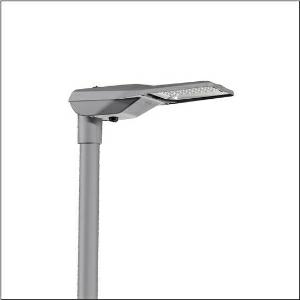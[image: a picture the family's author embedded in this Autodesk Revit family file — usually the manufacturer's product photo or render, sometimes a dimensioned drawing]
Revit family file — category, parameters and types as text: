
# Revit family: streetlight_sl_21_mini___st0_8a_5xe2c43t08jb_d1cf
name_source: partatom
category: Lighting Fixtures
units: mm (PartAtom-declared; Revit-internal decimal feet)

## family parameters
Cut with Voids When Loaded = No
Host = Face
Light Source = No
Part Type = Normal
Room Calculation Point = No
Round Connector Dimension = Use Diameter
Shared = No

## types (1)
- --- (1 x LED, 13500 lm, 88.6 W, 4000K)
    Apparent Load = 89 VA
    CIE Flux Codes = 41 75 97 100 100
    Color Rendering = 70
    Color Temperature = 4000K
    Default Elevation = 1800 mm
    Description = Streetlight SL 21 mini, mast luminaire, primary light control with lens, of PMMA, primary optical cover: cover, of toughened safety glass, transparent, light distribution: ST0.8a, light emission: direct distribution, primary light characteristic: asymmetric, installation type: side-entry, post-top, LED, High Power LED, rated luminous flux: 13.500lm, luminous efficacy: 152lm/W, light colour: 740, colour temperature: 4000K, control gear: D4i, control: overheat protection, constant luminous flux control, time-dependent luminous flux control, flexible luminous flux parameterisation, pre-setting: logarithmic dimming characteristic, mains connection: 220..240V, AC, 50/60Hz, start of lifetime: 89W, end of service life: 92W, reduction: 41W, luminaire housing, of diecast aluminium, powder-coated, Siteco® metallic grey (DB 702S), corrosivity category C5 mid according to DIN EN ISO 12944, please order mast flange separately, inclination adjustable: 0°, 5°, 10°, 15°, sealing non-destructively replaceable, multi-level sealing system, length: 628mm, width: 235mm, height: 110mm, mast flange for spigot size: 42mm (side-entry): 5XC10008XM4, 60/48mm (side-entry/post-top): 5XC10108XM2, 76/60mm (side-entry/post-top): 5XC10108XM1, mounting height: 4..8m, Smart Interface below and above, protection rating (complete): IP66, insulation class (complete): insulation class II (safety insulation), certification: CE, ENEC, ENEC+, VDE, impact resistance: IK10, permissible operating ambient temperature for outdoor applications: -40..+50°C, standard-compliant lighting for roads and squares, packaging unit: 1 piece

Light Distribution: ST0.8a
    Height = 110 mm
    Lamp = 1 x LED
    Lamp Light Flux = 13500 lm
    Lamp Power = 88.6 W
    Lamp count = 1
    Length = 625 mm
    Luminous efficacy = 152 lm/W
    Manufacturer = Siteco
    ModVariant = No
    Model = 5XE2C43T08JB
    Number of Poles = 1
    OnlyDefault = Yes
    Power Factor = 1
    Product Name = Streetlight SL 21 mini | ST0.8a
    Product group = mast luminaire | pylon top
    ProductGroupID = 6100
    Protection Class = Protection class II
    Protection Degree = IP 66
    RLX_Detail_Level = 1
    RLX_Emergency_Light_Flux = 0 lm
    RLX_Emergency_Type = 0
    RLX_Emergency_Type_DB = No
    RlxData = <blob elided: 26341 chars, md5=08f5da4b>
    Socket = socket
    Standby Power = 0 W
    System Light Flux = 13500 lm
    System Power = 89 W
    Type Comments = factory setting: luminous flux: 100 % | dim-lin: 254 | 915 mA
    Type Image = l_1003514.jpg
    URL = http://relux.com
    VarID = @adj_031021
    Voltage = 0 V
    Weight = 0.00 kg
    Width = 234 mm

## geometry (parser evidence)
native form markers: Blend x4, Sweep x10
no freeform markers — native parametric forms only
